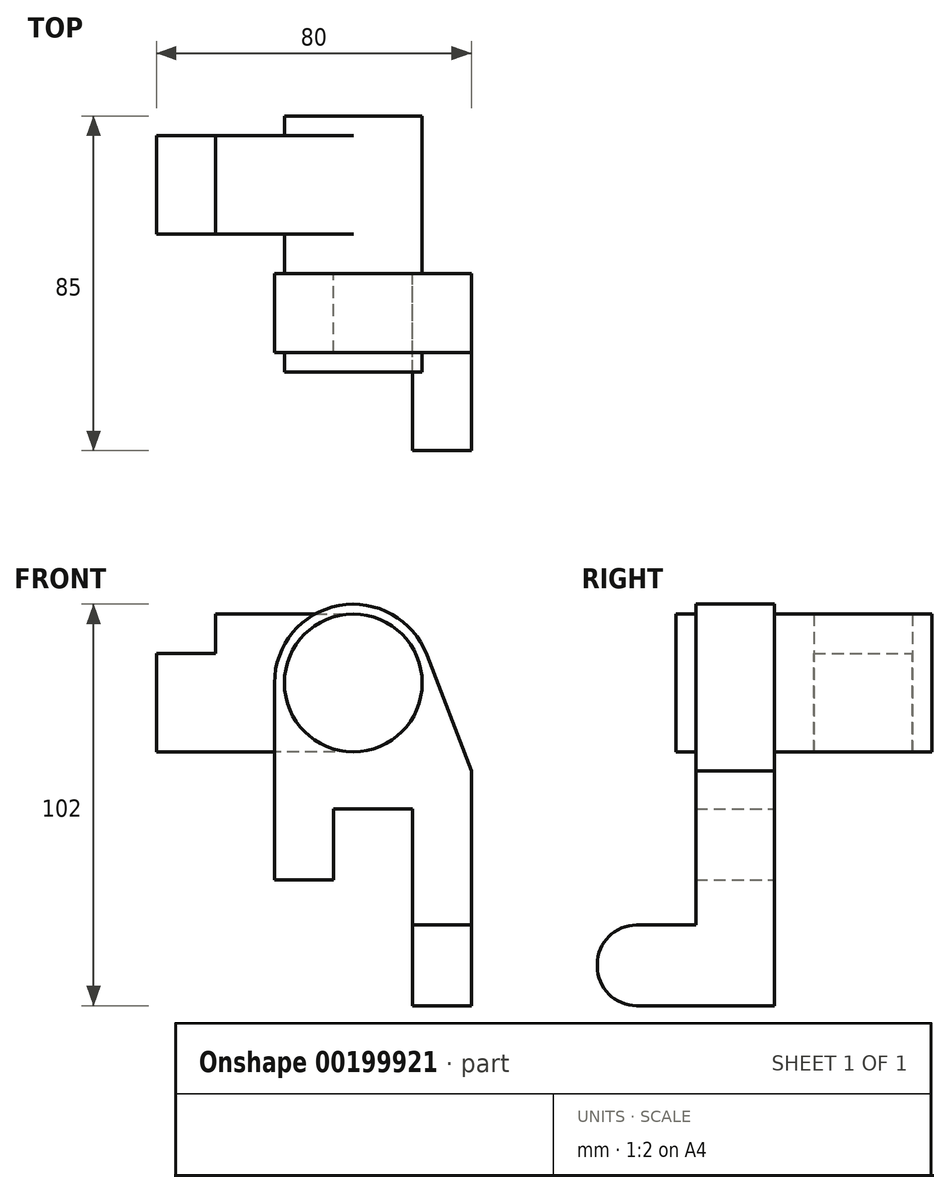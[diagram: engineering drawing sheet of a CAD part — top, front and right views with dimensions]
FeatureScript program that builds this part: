
annotation { "Feature Type Name" : "Feature", "Feature Type Description" : "" }
export const myFeature = defineFeature(function(context is Context, id is Id, definition is map)
    precondition{}
    {
        {
            var Q0;
            Q0=qCreatedBy(makeId("Front.planeOp"),FACE);
            var sketch = newSketch(context, id + "F0", { "sketchPlane" : qUnion([Q0])});
            skCircle(sketch, "E0", {"center": v(0, 0) * mm, "radius": 17.5 * mm});
            skCircle(sketch, "E1", {"center": v(0, 0) * mm, "radius": 20 * mm});
            skLineSegment(sketch, "E2", {"start": v(-20, 0) * mm, "end": v(-20, -50) * mm});
            skLineSegment(sketch, "E3", {"start": v(-20, -50) * mm, "end": v(-5, -50) * mm});
            skLineSegment(sketch, "E4", {"start": v(-5, -32) * mm, "end": v(-5, -50) * mm});
            skLineSegment(sketch, "E5", {"start": v(-5, -32) * mm, "end": v(15, -32) * mm});
            skLineSegment(sketch, "E6", {"start": v(15, -32) * mm, "end": v(15, -82) * mm});
            skLineSegment(sketch, "E7", {"start": v(15, -82) * mm, "end": v(30, -82) * mm});
            skLineSegment(sketch, "E8", {"start": v(30, -82) * mm, "end": v(30, -22.42) * mm});
            skLineSegment(sketch, "E9", {"start": v(30, -22.42) * mm, "end": v(18.68, 7.15) * mm});
            skLineSegment(sketch, "E10", {"start": v(15, -61.49) * mm, "end": v(30, -61.49) * mm});
            skSolve(sketch);
        }
        {
            var Q0;
            Q0 = qSketchRegion(id + "F0", true);
            extrude(context, id + "F1", {"entities" : qUnion([Q0]), "depth" : 20 * mm});
        }
        {
            var Q0;
            {var subQ0=sQuery(id+"F0.wireOp",EDGE,"E7");Q0=makeQuery(id+"F0.imprint","IMPRINT",FACE,{"disambiguationData":[TD([[makeQuery(id+"F0.imprint","IMPRINT",EDGE,{"derivedFrom":subQ0}),1.0]])]});}
            extrude(context, id + "F2", {"entities" : qUnion([Q0]), "operationType" : NewBodyOperationType.ADD, "depth" : 45 * mm});
        }
        {
            var Q0;
            Q0=makeQuery(id+"F0.imprint","IMPRINT",FACE,{"disambiguationData":[TD([[makeQuery(id+"F0.imprint","IMPRINT",EDGE,{"derivedFrom":sQuery(id+"F0.wireOp",EDGE,"E0")}),1.0]])]});
            extrude(context, id + "F3", {"entities" : qUnion([Q0]), "operationType" : NewBodyOperationType.ADD, "depth" : 25 * mm});
        }
        {
            var Q0;
            Q0=makeQuery(id+"F0.imprint","IMPRINT",FACE,{"disambiguationData":[TD([[makeQuery(id+"F0.imprint","IMPRINT",EDGE,{"derivedFrom":sQuery(id+"F0.wireOp",EDGE,"E0")}),1.0]])]});
            extrude(context, id + "F4", {"entities" : qUnion([Q0]), "operationType" : NewBodyOperationType.ADD, "oppositeDirection" : true, "depth" : 40 * mm});
        }
        {
            var Q0;
            Q0=makeQuery(id+"F2.opExtrude","CAP_EDGE",EDGE,{"disambiguationData":[OSD([sQuery(id+"F0.wireOp",EDGE,"E10")])],"isStart":false});
            var Q1;
            Q1=makeQuery(id+"F2.opExtrude","CAP_EDGE",EDGE,{"disambiguationData":[OSD([sQuery(id+"F0.wireOp",EDGE,"E7")])],"isStart":false});
            fillet(context, id + "F5", {"entities" : qUnion([Q0, Q1]), "radius" : 10 * mm, "tangentPropagation" : true, "allowEdgeOverflow" : false});
        }
        {
            var Q0;
            Q0=makeQuery(id+"F4.opExtrude","CAP_FACE",FACE,{"disambiguationData":[OSD([sQuery(id+"F0.wireOp",EDGE,"E0")])],"isStart":false});
            var sketch = newSketch(context, id + "F6", { "sketchPlane" : qUnion([Q0])});
            skLineSegment(sketch, "E11", {"start": v(0, 17.5) * mm, "end": v(0, -17.5) * mm});
            skLineSegment(sketch, "E12", {"start": v(0, -17.5) * mm, "end": v(50, -17.5) * mm});
            skLineSegment(sketch, "E13", {"start": v(50, -17.5) * mm, "end": v(50, 17.5) * mm});
            skLineSegment(sketch, "E14", {"start": v(50, 17.5) * mm, "end": v(0, 17.5) * mm});
            skLineSegment(sketch, "E15", {"start": v(35, 17.5) * mm, "end": v(50, 17.5) * mm});
            skLineSegment(sketch, "E16", {"start": v(35, 17.5) * mm, "end": v(35, 7.5) * mm});
            skLineSegment(sketch, "E17", {"start": v(35, 7.5) * mm, "end": v(50, 7.5) * mm});
            skSolve(sketch);
        }
        {
            var Q0;
            {var subQ2=sQuery(id+"F6.wireOp",EDGE,"E12");Q0=makeQuery(id+"F6.imprint","IMPRINT",FACE,{"disambiguationData":[TD([[makeQuery(id+"F6.imprint","IMPRINT",EDGE,{"derivedFrom":subQ2}),1.0]])]});}
            extrude(context, id + "F7", {"entities" : qUnion([Q0]), "operationType" : NewBodyOperationType.ADD, "oppositeDirection" : true, "depth" : 30 * mm});
        }
        {
            var Q0;
            {var subQ2=sQuery(id+"F6.wireOp",EDGE,"E12");Q0=makeQuery(id+"F6.imprint","IMPRINT",FACE,{"disambiguationData":[TD([[makeQuery(id+"F6.imprint","IMPRINT",EDGE,{"derivedFrom":subQ2}),1.0]])]});}
            extrude(context, id + "F8", {"entities" : qUnion([Q0]), "operationType" : NewBodyOperationType.REMOVE, "oppositeDirection" : true, "depth" : 5 * mm});
        }
    });
